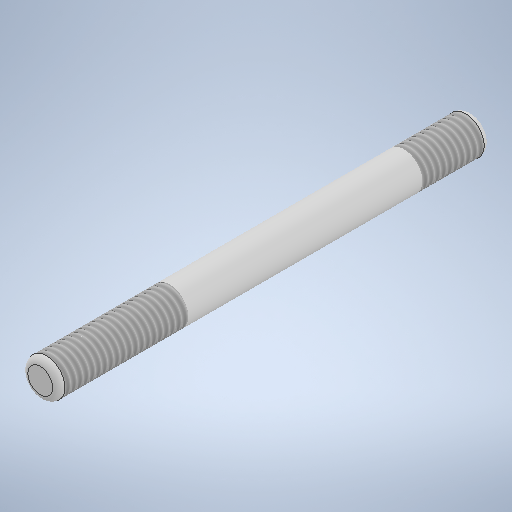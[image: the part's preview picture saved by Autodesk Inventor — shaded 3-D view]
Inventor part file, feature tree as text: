
AUTODESK INVENTOR PART (.ipt)
format: ipt  version: 2025.1 (Build 291241000, 241)  size: 291,328 bytes
history: native  units: mm
features: thread x2, extrude x1, fillet x1, sketch x1
ambient origin geometry x8: Origin, YZ Plane, XZ Plane, XY Plane, X Axis, Y Axis, Z Axis, Center Point
bodies: Solid1 (feature_tree)
feature tree (5):
  extrude  "Extrusion1"  Depth=35.0mm TaperAngle=0.0deg
  fillet  "Fillet1"  Radius=0.5mm
  thread  "Thread1"  [1 undecoded]
  thread  "Thread2"  [1 undecoded]
  sketch  "Sketch1"  dims[d0=3.0mm d1=35.0mm d2=0.0mm d3=0.5mm d4=10.0mm d5=0.0mm d6=5.0mm d7=0.0mm]
note: 2 required parameter values undecoded (feature->parameter linkage not recoverable at this tier; creation-order binding heuristic only, values carry confidence <= 0.55)
